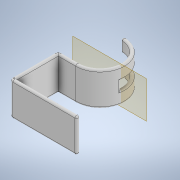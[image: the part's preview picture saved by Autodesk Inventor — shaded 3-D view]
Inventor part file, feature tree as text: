
AUTODESK INVENTOR PART (.ipt)
format: ipt  version: 2020 (Build 240168000, 168)  size: 215,552 bytes
history: native  units: in
note: dims shown in document units (in); Inventor stores cm internally (conversion verified against a paired STEP export)
features: fillet x4, extrude x2, sketch x2, plane x1
ambient origin geometry x8: Origin, YZ Plane, XZ Plane, XY Plane, X Axis, Y Axis, Z Axis, Center Point
bodies: Solid1 (feature_tree)
feature tree (9):
  extrude  "Extrusion1"  Depth=0.0787in
  fillet  "Fillet1"  Radius=0.0787in
  fillet  "Fillet2"  Radius=0.9843in
  fillet  "Fillet3"  Radius=0.9843in
  plane  "Work Plane1"
  extrude  "Extrusion2"  Depth=0.0394in
  fillet  "Fillet4"  Radius=0.0787in
  sketch  "Sketch1"  dims[d0=1.5748in d1=0.0787in d2=0.0787in d3=0.9843in d4=0.9843in]
  sketch  "Sketch3"  dims[d5=0.0787in d6=0.9843in d7=0.0787in d8=0.0787in d9=0.7874in d10=0.0in d11=0.0787in d12=0.0394in d13=0.0394in d14=-1.5625in d15=0.0984in d16=0.1969in d17=0.7874in d18=0.0in d19=0.0394in]
